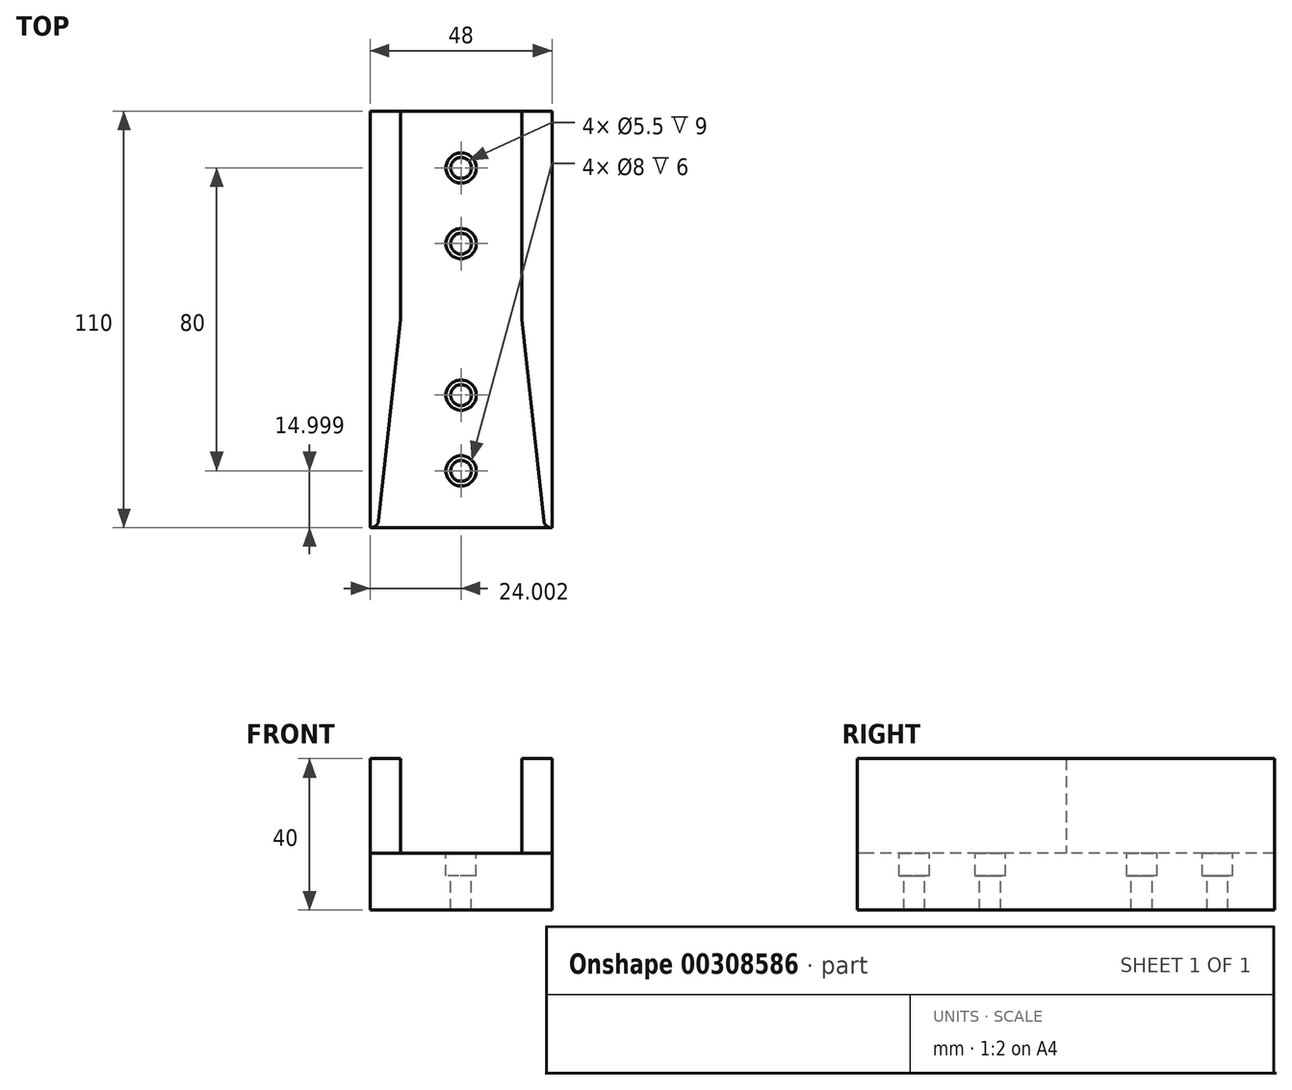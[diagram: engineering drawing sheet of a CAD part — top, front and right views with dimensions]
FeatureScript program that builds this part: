
annotation { "Feature Type Name" : "Feature", "Feature Type Description" : "" }
export const myFeature = defineFeature(function(context is Context, id is Id, definition is map)
    precondition{}
    {
        {
            var Q0;
            Q0=qCreatedBy(makeId("Top.planeOp"),FACE);
            var sketch = newSketch(context, id + "F0", { "sketchPlane" : qUnion([Q0])});
            skLineSegment(sketch, "E0.bottom", {"start": v(-14.28, 77.83) * mm, "end": v(33.72, 77.83) * mm});
            skLineSegment(sketch, "E0.top", {"start": v(-14.28, -32.17) * mm, "end": v(33.72, -32.17) * mm});
            skLineSegment(sketch, "E0.left", {"start": v(-14.28, 77.83) * mm, "end": v(-14.28, -32.17) * mm});
            skLineSegment(sketch, "E0.right", {"start": v(33.72, 77.83) * mm, "end": v(33.72, -32.17) * mm});
            skSolve(sketch);
        }
        {
            var Q0;
            Q0=makeQuery(id+"F0.imprint","IMPRINT",FACE,{"disambiguationData":[TD([[makeQuery(id+"F0.imprint","IMPRINT",EDGE,{"derivedFrom":sQuery(id+"F0.wireOp",EDGE,"E0.bottom")}),-1.0]])]});
            extrude(context, id + "F1", {"entities" : qUnion([Q0]), "endBound" : BoundingType.SYMMETRIC, "depth" : 15 * mm});
        }
        {
            var Q0;
            Q0=makeQuery(id+"F1.opExtrude","CAP_FACE",FACE,{"disambiguationData":[OSD([sQuery(id+"F0.wireOp",EDGE,"E0.bottom"),sQuery(id+"F0.wireOp",EDGE,"E0.top"),sQuery(id+"F0.wireOp",EDGE,"E0.left"),sQuery(id+"F0.wireOp",EDGE,"E0.right")])],"isStart":true});
            var sketch = newSketch(context, id + "F2", { "sketchPlane" : qUnion([Q0])});
            skLineSegment(sketch, "E1", {"start": v(9.72, 32.17) * mm, "end": v(9.72, -77.83) * mm, "construction": true});
            skLineSegment(sketch, "E2", {"start": v(33.72, -22.83) * mm, "end": v(-14.28, -22.83) * mm, "construction": true});
            skLineSegment(sketch, "E3.bottom", {"start": v(24.72, 7.17) * mm, "end": v(-5.28, 7.17) * mm});
            skLineSegment(sketch, "E3.top", {"start": v(24.72, -52.83) * mm, "end": v(-5.28, -52.83) * mm});
            skLineSegment(sketch, "E3.left", {"start": v(24.72, 7.17) * mm, "end": v(24.72, -52.83) * mm});
            skLineSegment(sketch, "E3.right", {"start": v(-5.28, 7.17) * mm, "end": v(-5.28, -52.83) * mm});
            skPoint(sketch, "E3.middle", {"position": v(9.72, -22.83) * mm});
            skSolve(sketch);
        }
        {
            var Q0;
            Q0=makeQuery(id+"F1.opExtrude","CAP_FACE",FACE,{"disambiguationData":[OSD([sQuery(id+"F0.wireOp",EDGE,"E0.bottom"),sQuery(id+"F0.wireOp",EDGE,"E0.top"),sQuery(id+"F0.wireOp",EDGE,"E0.left"),sQuery(id+"F0.wireOp",EDGE,"E0.right")])],"isStart":false});
            var sketch = newSketch(context, id + "F3", { "sketchPlane" : qUnion([Q0])});
            skLineSegment(sketch, "E4", {"start": v(-6.28, 77.83) * mm, "end": v(-6.28, 22.83) * mm});
            skLineSegment(sketch, "E5", {"start": v(25.72, 77.83) * mm, "end": v(25.72, 22.83) * mm});
            skLineSegment(sketch, "E6", {"start": v(-14.28, 22.83) * mm, "end": v(33.72, 22.83) * mm, "construction": true});
            skLineSegment(sketch, "E7", {"start": v(33.72, 52.22) * mm, "end": v(-14.28, 52.22) * mm, "construction": true});
            skLineSegment(sketch, "E8", {"start": v(-14.28, -8.35) * mm, "end": v(33.72, -8.35) * mm, "construction": true});
            skPoint(sketch, "E9.trimOffspring.end.orphan", {"position": v(-6.28, -32.17) * mm});
            skPoint(sketch, "E10.orphan", {"position": v(25.72, -32.17) * mm});
            skPoint(sketch, "E11", {"position": v(-12.28, -32.17) * mm});
            skPoint(sketch, "E12", {"position": v(31.72, -32.17) * mm});
            skLineSegment(sketch, "E13", {"start": v(-6.28, 22.83) * mm, "end": v(-12.08, -30.39) * mm});
            skLineSegment(sketch, "E14", {"start": v(25.72, 22.83) * mm, "end": v(31.53, -30.39) * mm});
            skLineSegment(sketch, "E15", {"start": v(-14.28, -32.17) * mm, "end": v(-14.07, -32.17) * mm});
            skLineSegment(sketch, "E16", {"start": v(33.52, -32.17) * mm, "end": v(33.72, -32.17) * mm});
            skArc(sketch, "E17.filletArc", {"start": v(-14.07, -32.17) * mm, "mid": v(-12.74, -31.66) * mm, "end": v(-12.08, -30.39) * mm});
            skArc(sketch, "E18.filletArc", {"start": v(31.53, -30.39) * mm, "mid": v(32.18, -31.66) * mm, "end": v(33.52, -32.17) * mm});
            skSolve(sketch);
        }
        {
            var Q0;
            {var subQ0=sQuery(id+"F3.wireOp",EDGE,"E4");Q0=makeQuery(id+"F3.imprint","IMPRINT",FACE,{"disambiguationData":[TD([[makeQuery(id+"F3.imprint","IMPRINT",EDGE,{"derivedFrom":subQ0}),-1.0]])]});}
            var Q1;
            {var subQ0=sQuery(id+"F3.wireOp",EDGE,"E5");Q1=makeQuery(id+"F3.imprint","IMPRINT",FACE,{"disambiguationData":[TD([[makeQuery(id+"F3.imprint","IMPRINT",EDGE,{"derivedFrom":subQ0}),1.0]])]});}
            extrude(context, id + "F4", {"entities" : qUnion([Q0, Q1]), "operationType" : NewBodyOperationType.ADD, "depth" : 25 * mm});
        }
        {
            var Q0;
            Q0=makeQuery(id+"F1.opExtrude","CAP_FACE",FACE,{"disambiguationData":[OSD([sQuery(id+"F0.wireOp",EDGE,"E0.bottom"),sQuery(id+"F0.wireOp",EDGE,"E0.top"),sQuery(id+"F0.wireOp",EDGE,"E0.left"),sQuery(id+"F0.wireOp",EDGE,"E0.right")])],"isStart":false});
            var sketch = newSketch(context, id + "F5", { "sketchPlane" : qUnion([Q0])});
            skLineSegment(sketch, "E19", {"start": v(9.72, -32.17) * mm, "end": v(9.72, 77.83) * mm, "construction": true});
            skPoint(sketch, "E20", {"position": v(9.72, 42.83) * mm});
            skPoint(sketch, "E21", {"position": v(9.72, 62.83) * mm});
            skPoint(sketch, "E22", {"position": v(9.72, -17.17) * mm});
            skPoint(sketch, "E23", {"position": v(9.72, 2.83) * mm});
            skSolve(sketch);
        }
        {
            var Q0;
            Q0=sQuery(id+"F5.wireOp",VERTEX,"E20");
            var Q1;
            Q1=sQuery(id+"F5.wireOp",VERTEX,"E21");
            var Q2;
            Q2=sQuery(id+"F5.wireOp",VERTEX,"E23");
            var Q3;
            Q3=sQuery(id+"F5.wireOp",VERTEX,"E22");
            var Q4;
            Q4=makeQuery(id+"F1.opExtrude","SWEPT_BODY",BODY,{"disambiguationData":[OSD([sQuery(id+"F0.wireOp",EDGE,"E0.bottom"),sQuery(id+"F0.wireOp",EDGE,"E0.top"),sQuery(id+"F0.wireOp",EDGE,"E0.left"),sQuery(id+"F0.wireOp",EDGE,"E0.right")])]});
            hole(context, id + "F6", {"style" : HoleStyle.C_BORE, "endStyle" : HoleEndStyle.THROUGH, "holeDiameter" : 5.5 * mm, "cBoreDiameter" : 8 * mm, "cBoreDepth" : 6 * mm, "tappedDepth" : 12 * mm, "tapClearance" : 3, "locations" : qUnion([Q0, Q1, Q2, Q3]), "scope" : qUnion([Q4])});
        }
    });
